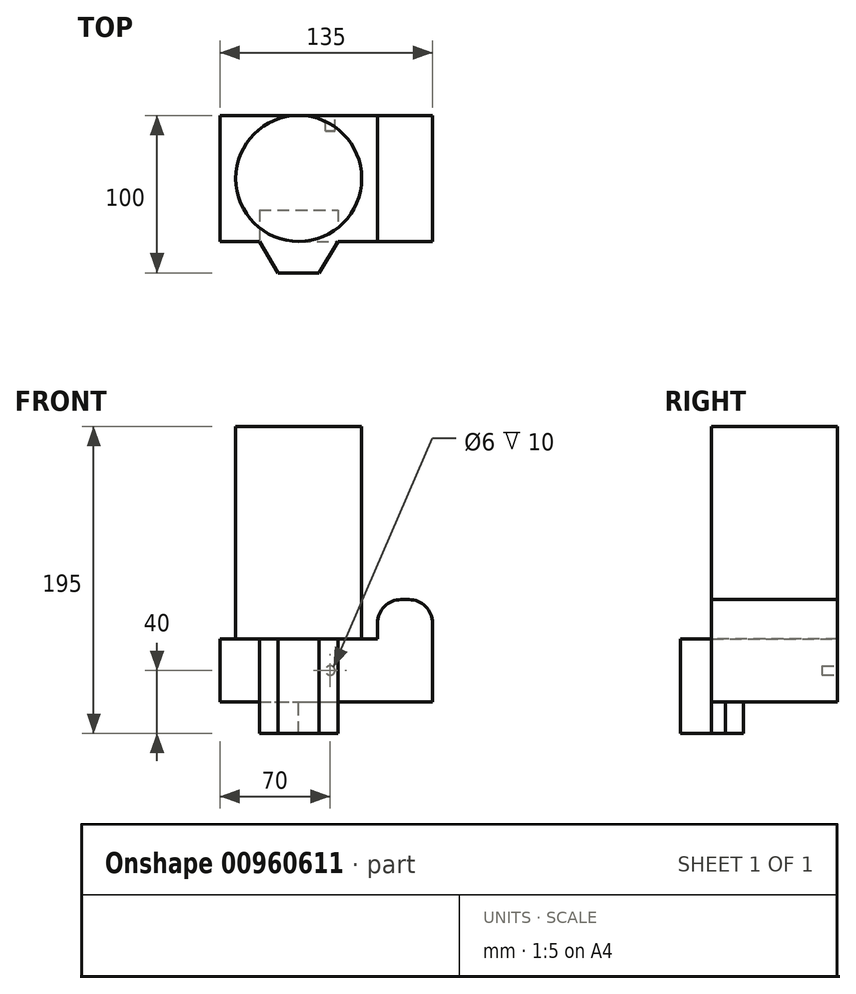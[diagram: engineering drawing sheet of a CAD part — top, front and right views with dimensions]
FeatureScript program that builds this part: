
annotation { "Feature Type Name" : "Feature", "Feature Type Description" : "" }
export const myFeature = defineFeature(function(context is Context, id is Id, definition is map)
    precondition{}
    {
        {
            var Q0;
            Q0=qCreatedBy(makeId("Front.planeOp"),FACE);
            var sketch = newSketch(context, id + "F0", { "sketchPlane" : qUnion([Q0])});
            skLineSegment(sketch, "E0", {"start": v(0, 0) * mm, "end": v(0, 50) * mm});
            skLineSegment(sketch, "E1", {"start": v(-15, 65) * mm, "end": v(-20, 65) * mm});
            skLineSegment(sketch, "E2", {"start": v(-35, 50) * mm, "end": v(-35, 40) * mm});
            skLineSegment(sketch, "E3", {"start": v(-35, 40) * mm, "end": v(-135, 40) * mm});
            skLineSegment(sketch, "E4", {"start": v(-135, 40) * mm, "end": v(-135, 0) * mm});
            skLineSegment(sketch, "E5", {"start": v(-135, 0) * mm, "end": v(0, 0) * mm});
            skPoint(sketch, "E6.visualSharp", {"position": v(-35, 65) * mm});
            skArc(sketch, "E6.filletArc", {"start": v(-20, 65) * mm, "mid": v(-30.6, 60.6) * mm, "end": v(-35, 50) * mm});
            skPoint(sketch, "E7.visualSharp", {"position": v(0, 65) * mm});
            skArc(sketch, "E7.filletArc", {"start": v(0, 50) * mm, "mid": v(-4.4, 60.6) * mm, "end": v(-15, 65) * mm});
            skSolve(sketch);
        }
        {
            var Q0;
            Q0=makeQuery(id+"F0.imprint","IMPRINT",FACE,{"disambiguationData":[TD([[makeQuery(id+"F0.imprint","IMPRINT",EDGE,{"derivedFrom":sQuery(id+"F0.wireOp",EDGE,"E0")}),1.0]])]});
            extrude(context, id + "F1", {"entities" : qUnion([Q0]), "depth" : 80 * mm, "offsetDistance" : 25 * mm});
        }
        {
            var Q0;
            Q0=makeQuery(id+"F1.opExtrude","SWEPT_FACE",FACE,{"disambiguationData":[OSD([sQuery(id+"F0.wireOp",EDGE,"E3")])]});
            var sketch = newSketch(context, id + "F2", { "sketchPlane" : qUnion([Q0])});
            skLineSegment(sketch, "E8.0.0", {"start": v(-35, 0) * mm, "end": v(-135, 0) * mm});
            skLineSegment(sketch, "E8.0.1", {"start": v(-135, 0) * mm, "end": v(-135, -80) * mm});
            skLineSegment(sketch, "E8.0.2", {"start": v(-135, -80) * mm, "end": v(-35, -80) * mm});
            skLineSegment(sketch, "E8.0.3", {"start": v(-35, -80) * mm, "end": v(-35, 0) * mm});
            skCircle(sketch, "E9", {"center": v(-85, -40) * mm, "radius": 40 * mm});
            skSolve(sketch);
        }
        {
            var Q0;
            {var subQ0=sQuery(id+"F2.wireOp",EDGE,"E9");var subQ1=makeQuery(id+"F2.imprint","INTERSECT",VERTEX,{"derivedFrom":[sQuery(id+"F2.wireOp",EDGE,"E8.0.0"),subQ0]});Q0=makeQuery(id+"F2.imprint","IMPRINT",FACE,{"disambiguationData":[TD([[makeQuery(id+"F2.imprint","IMPRINT",EDGE,{"disambiguationData":[TD([[subQ1,-1.0]])],"derivedFrom":subQ0}),1.0]])]});}
            extrude(context, id + "F3", {"entities" : qUnion([Q0]), "operationType" : NewBodyOperationType.ADD, "depth" : 135 * mm, "offsetDistance" : 25 * mm});
        }
        {
            var Q0;
            {var subQ0=sQuery(id+"F0.wireOp",EDGE,"E3");var subQ1=makeQuery(id+"F1.opExtrude","SWEPT_FACE",FACE,{"disambiguationData":[OSD([subQ0])]});var subQ2=sQuery(id+"F0.wireOp",EDGE,"E2");Q0=makeQuery(id+"F3.boolean.opBoolean","SPLIT",FACE,{"disambiguationData":[TD([makeQuery(id+"F1.opExtrude","SWEPT_FACE",FACE,{"disambiguationData":[OSD([subQ2])]})])],"derivedFrom":subQ1});}
            var sketch = newSketch(context, id + "F4", { "sketchPlane" : qUnion([Q0])});
            skLineSegment(sketch, "E10.bottom", {"start": v(-110, -60) * mm, "end": v(-60, -60) * mm});
            skLineSegment(sketch, "E10.top", {"start": v(-110, -100) * mm, "end": v(-60, -100) * mm});
            skLineSegment(sketch, "E10.left", {"start": v(-110, -60) * mm, "end": v(-110, -100) * mm});
            skLineSegment(sketch, "E10.right", {"start": v(-60, -60) * mm, "end": v(-60, -100) * mm});
            skPoint(sketch, "E10.middle", {"position": v(-85, -80) * mm});
            skLineSegment(sketch, "E11", {"start": v(-110, -80) * mm, "end": v(-98, -100) * mm});
            skLineSegment(sketch, "E12", {"start": v(-60, -80) * mm, "end": v(-72, -100) * mm});
            skSolve(sketch);
        }
        {
            var Q0;
            {var subQ1=sQuery(id+"F4.wireOp",EDGE,"E10.bottom");Q0=makeQuery(id+"F4.imprint","IMPRINT",FACE,{"disambiguationData":[TD([[makeQuery(id+"F4.imprint","IMPRINT",EDGE,{"derivedFrom":subQ1}),-1.0]])]});}
            var Q1;
            {var subQ0=sQuery(id+"F4.wireOp",EDGE,"E10.right");var subQ3=sQuery(id+"F2.wireOp",EDGE,"E9");var subQ6=makeQuery(id+"F3.boolean.opBoolean","SPLIT",EDGE,{"disambiguationData":[OD(0.0)],"derivedFrom":makeQuery(id+"F3.opExtrude","CAP_EDGE",EDGE,{"disambiguationData":[OSD([subQ3])],"isStart":true})});var subQ7=makeQuery(id+"F4.imprint","INTERSECT",VERTEX,{"derivedFrom":[subQ6,subQ0]});Q1=makeQuery(id+"F4.imprint","IMPRINT",FACE,{"disambiguationData":[TD([[makeQuery(id+"F4.imprint","IMPRINT",EDGE,{"disambiguationData":[TD([[subQ7,1.0]])],"derivedFrom":subQ6}),-1.0]])]});}
            extrude(context, id + "F5", {"entities" : qUnion([Q0, Q1]), "operationType" : NewBodyOperationType.ADD, "oppositeDirection" : true, "depth" : 60 * mm, "offsetDistance" : 25 * mm});
        }
        {
            var Q0;
            Q0=makeQuery(id+"F1.opExtrude","CAP_FACE",FACE,{"disambiguationData":[OSD([sQuery(id+"F0.wireOp",EDGE,"E0"),sQuery(id+"F0.wireOp",EDGE,"E1"),sQuery(id+"F0.wireOp",EDGE,"E2"),sQuery(id+"F0.wireOp",EDGE,"E3"),sQuery(id+"F0.wireOp",EDGE,"E4"),sQuery(id+"F0.wireOp",EDGE,"E5"),sQuery(id+"F0.wireOp",EDGE,"E6.filletArc"),sQuery(id+"F0.wireOp",EDGE,"E7.filletArc")])],"isStart":true});
            var sketch = newSketch(context, id + "F6", { "sketchPlane" : qUnion([Q0])});
            skCircle(sketch, "E13", {"center": v(65, 20) * mm, "radius": 3 * mm});
            skSolve(sketch);
        }
        {
            var Q0;
            Q0=makeQuery(id+"F6.imprint","IMPRINT",FACE,{"disambiguationData":[TD([[makeQuery(id+"F6.imprint","IMPRINT",EDGE,{"derivedFrom":sQuery(id+"F6.wireOp",EDGE,"E13")}),1.0]])]});
            extrude(context, id + "F7", {"entities" : qUnion([Q0]), "operationType" : NewBodyOperationType.REMOVE, "oppositeDirection" : true, "depth" : 10 * mm, "offsetDistance" : 25 * mm});
        }
    });
